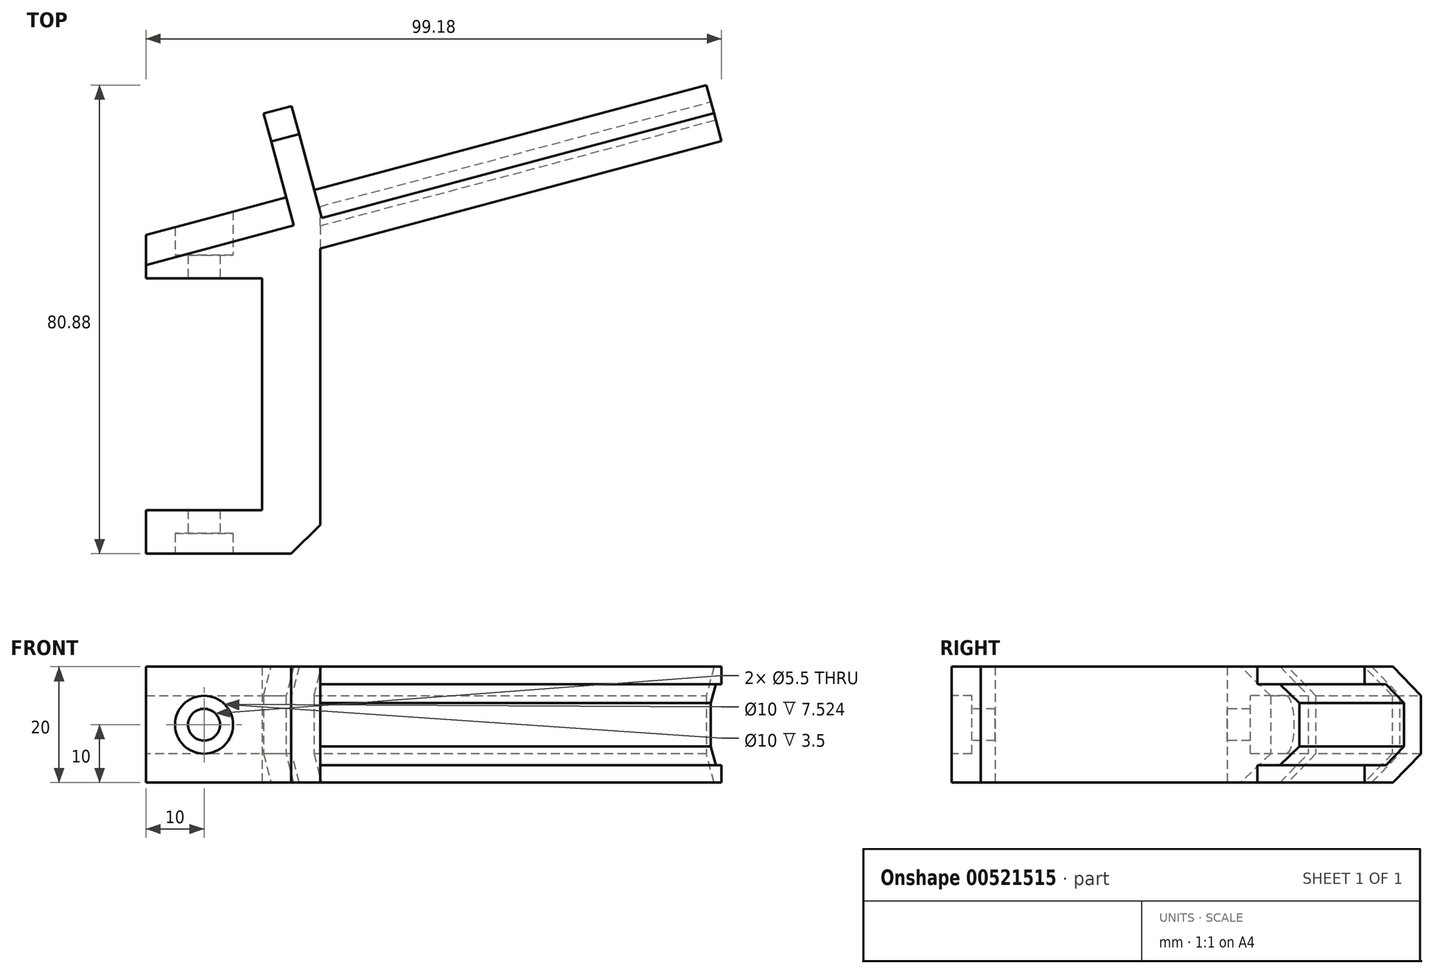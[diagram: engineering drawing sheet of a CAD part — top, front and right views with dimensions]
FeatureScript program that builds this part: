
annotation { "Feature Type Name" : "Feature", "Feature Type Description" : "" }
export const myFeature = defineFeature(function(context is Context, id is Id, definition is map)
    precondition{}
    {
        {
            var Q0;
            Q0=qCreatedBy(makeId("Top.planeOp"),FACE);
            var sketch = newSketch(context, id + "F0", { "sketchPlane" : qUnion([Q0])});
            skLineSegment(sketch, "E0", {"start": v(0, 0) * mm, "end": v(24.15, 6.47) * mm});
            skLineSegment(sketch, "E1", {"start": v(24.15, 6.47) * mm, "end": v(20.27, 20.96) * mm});
            skLineSegment(sketch, "E2", {"start": v(20.27, 20.96) * mm, "end": v(25.1, 22.25) * mm});
            skLineSegment(sketch, "E3", {"start": v(25.1, 22.25) * mm, "end": v(28.98, 7.76) * mm});
            skLineSegment(sketch, "E4", {"start": v(28.98, 7.76) * mm, "end": v(96.6, 25.88) * mm});
            skLineSegment(sketch, "E5", {"start": v(96.6, 25.88) * mm, "end": v(99.18, 16.22) * mm});
            skLineSegment(sketch, "E6", {"start": v(0, -55) * mm, "end": v(0, -47.5) * mm});
            skLineSegment(sketch, "E7", {"start": v(0, -47.5) * mm, "end": v(20, -47.5) * mm});
            skLineSegment(sketch, "E8", {"start": v(20, -47.5) * mm, "end": v(20, -7.5) * mm});
            skLineSegment(sketch, "E9", {"start": v(20, -7.5) * mm, "end": v(0, -7.5) * mm});
            skLineSegment(sketch, "E10", {"start": v(0, -7.5) * mm, "end": v(0, 0) * mm});
            skLineSegment(sketch, "E11", {"start": v(0, -55) * mm, "end": v(25, -55) * mm});
            skLineSegment(sketch, "E12", {"start": v(25, -55) * mm, "end": v(30, -50) * mm});
            skLineSegment(sketch, "E13", {"start": v(30, -50) * mm, "end": v(30, -2.31) * mm});
            skLineSegment(sketch, "E14", {"start": v(30, -2.31) * mm, "end": v(99.18, 16.22) * mm});
            skSolve(sketch);
        }
        {
            var Q0;
            Q0 = qSketchRegion(id + "F0", true);
            extrude(context, id + "F1", {"entities" : qUnion([Q0]), "depth" : 20 * mm, "offsetDistance" : 25 * mm});
        }
        {
            var Q0;
            Q0=makeQuery(id+"F1.opExtrude","SWEPT_FACE",FACE,{"disambiguationData":[OSD([sQuery(id+"F0.wireOp",EDGE,"E11")])]});
            var sketch = newSketch(context, id + "F2", { "sketchPlane" : qUnion([Q0])});
            skCircle(sketch, "E15", {"center": v(10, 10) * mm, "radius": 2.75 * mm});
            skPoint(sketch, "E15.centerSnap0", {"position": v(0, 10) * mm});
            skPoint(sketch, "E15.centerSnap1", {"position": v(12.5, 20) * mm});
            skPoint(sketch, "E16.0", {"position": v(10, 20) * mm});
            skSolve(sketch);
        }
        {
            var Q0;
            Q0 = qSketchRegion(id + "F2", true);
            extrude(context, id + "F3", {"entities" : qUnion([Q0]), "operationType" : NewBodyOperationType.REMOVE, "endBound" : BoundingType.THROUGH_ALL, "oppositeDirection" : true, "depth" : 25 * mm, "offsetDistance" : 25 * mm});
        }
        {
            var Q0;
            Q0=makeQuery(id+"F1.opExtrude","SWEPT_FACE",FACE,{"disambiguationData":[OSD([sQuery(id+"F0.wireOp",EDGE,"E9")])]});
            cPlane(context, id + "F4", {"entities" : qUnion([Q0]), "cplaneType" : CPlaneType.OFFSET, "offset" : 4 * mm, "oppositeDirection" : true, "width" : 150 * mm, "height" : 150 * mm});
        }
        {
            var Q0;
            Q0=qCreatedBy(id+"F4.planeOp",FACE);
            var sketch = newSketch(context, id + "F5", { "sketchPlane" : qUnion([Q0])});
            skCircle(sketch, "E17.0", {"center": v(10, 10) * mm, "radius": 2.75 * mm, "construction": true});
            skCircle(sketch, "E18", {"center": v(10, 10) * mm, "radius": 5 * mm});
            skSolve(sketch);
        }
        {
            var Q0;
            Q0 = qSketchRegion(id + "F5", true);
            extrude(context, id + "F6", {"entities" : qUnion([Q0]), "operationType" : NewBodyOperationType.REMOVE, "endBound" : BoundingType.THROUGH_ALL, "oppositeDirection" : true, "depth" : 25 * mm, "offsetDistance" : 25 * mm});
        }
        {
            var Q0;
            Q0=makeQuery(id+"F1.opExtrude","SWEPT_FACE",FACE,{"disambiguationData":[OSD([sQuery(id+"F0.wireOp",EDGE,"E11")])]});
            var sketch = newSketch(context, id + "F7", { "sketchPlane" : qUnion([Q0])});
            skCircle(sketch, "E19", {"center": v(10, 10) * mm, "radius": 5 * mm});
            skSolve(sketch);
        }
        {
            var Q0;
            Q0 = qSketchRegion(id + "F7", true);
            extrude(context, id + "F8", {"entities" : qUnion([Q0]), "operationType" : NewBodyOperationType.REMOVE, "oppositeDirection" : true, "depth" : 3.5 * mm, "offsetDistance" : 25 * mm});
        }
        {
            var Q0;
            Q0=makeQuery(id+"F1.opExtrude","CAP_EDGE",EDGE,{"disambiguationData":[OSD([sQuery(id+"F0.wireOp",EDGE,"E4")])],"isStart":true});
            var Q1;
            Q1=makeQuery(id+"F1.opExtrude","CAP_EDGE",EDGE,{"disambiguationData":[OSD([sQuery(id+"F0.wireOp",EDGE,"E4")])],"isStart":false});
            var Q2;
            Q2=makeQuery(id+"F1.opExtrude","CAP_EDGE",EDGE,{"disambiguationData":[OSD([sQuery(id+"F0.wireOp",EDGE,"E0")])],"isStart":false});
            var Q3;
            Q3=makeQuery(id+"F1.opExtrude","CAP_EDGE",EDGE,{"disambiguationData":[OSD([sQuery(id+"F0.wireOp",EDGE,"E0")])],"isStart":true});
            var Q4;
            Q4=makeQuery(id+"F1.opExtrude","CAP_EDGE",EDGE,{"disambiguationData":[OSD([sQuery(id+"F0.wireOp",EDGE,"E2")])],"isStart":false});
            var Q5;
            Q5=makeQuery(id+"F1.opExtrude","CAP_EDGE",EDGE,{"disambiguationData":[OSD([sQuery(id+"F0.wireOp",EDGE,"E2")])],"isStart":true});
            chamfer(context, id + "F9", {"entities" : qUnion([Q0, Q1, Q2, Q3, Q4, Q5]), "width" : 5 * mm, "tangentPropagation" : true});
        }
        {
            var Q0;
            Q0=makeQuery(id+"F1.opExtrude","SWEPT_FACE",FACE,{"disambiguationData":[OSD([sQuery(id+"F0.wireOp",EDGE,"E5")])]});
            var sketch = newSketch(context, id + "F10", { "sketchPlane" : qUnion([Q0])});
            skLineSegment(sketch, "E20.0", {"start": v(-6.24, 17) * mm, "end": v(-15, 17) * mm});
            skLineSegment(sketch, "E20.1", {"start": v(-6.24, 3) * mm, "end": v(-15, 3) * mm});
            skLineSegment(sketch, "E20.2", {"start": v(-6.24, 3) * mm, "end": v(-3, 6.24) * mm});
            skLineSegment(sketch, "E20.3", {"start": v(-3, 13.76) * mm, "end": v(-3, 6.24) * mm});
            skLineSegment(sketch, "E20.4", {"start": v(-3, 13.76) * mm, "end": v(-6.24, 17) * mm});
            skLineSegment(sketch, "E21", {"start": v(-15, 17) * mm, "end": v(-15, 3) * mm});
            skSolve(sketch);
        }
        {
            var Q0;
            Q0 = qSketchRegion(id + "F10", true);
            var Q1;
            Q1=makeQuery(id+"F1.opExtrude","SWEPT_FACE",FACE,{"disambiguationData":[OSD([sQuery(id+"F0.wireOp",EDGE,"E13")])]});
            extrude(context, id + "F11", {"entities" : qUnion([Q0]), "operationType" : NewBodyOperationType.REMOVE, "endBound" : BoundingType.UP_TO_SURFACE, "oppositeDirection" : true, "depth" : 25 * mm, "endBoundEntityFace" : qUnion([Q1]), "offsetDistance" : 25 * mm});
        }
    });
